# Revit family: Kee_Safety_INTEW010_-_KEELINE_EXTENDED_INT_BRACKET
name_source: partatom
category: Generic Models
units: mm (PartAtom-declared; Revit-internal decimal feet)

## family parameters
Can host rebar = No
Cut with Voids When Loaded = No
Host = Face
Maintain Annotation Orientation = No
Part Type = Normal
Room Calculation Point = No
Round Connector Dimension = Use Diameter
Shared = No

## types (1)
- Kee_Safety_INTEW010_-_KEELINE_EXTENDED_INT_BRACKET
    Assembly Code = INTEW010
    CE Approval = Yes
    Colour = Natural
    Coverage Area = 0 m²
    Default Elevation = 1219 mm
    Design Country = United Kingdom
    Finish = Natural
    Gross Weight kg = 0.63
    Location of Manufacturer = Cradley Heath
    Manufacturer = Kee Safety
    Manufacturer Country = United Kingdom
    Manufacturer Website = www.keesafety.co.uk
    Material = Stainless Steel, Polished
    Overall Height = 88 mm
    Overall Length = 442 mm
    Overall Width = 45 mm  [stored 0.147638 ft]
    Product Family = KeeLine
    Product Group = KeeLine
    Product Model Number = LAINTEXT0
    Product Range = KeeLine
    Shipping Weight kg = 0.0
    Width = 45 mm  [stored 0.147638 ft]

note: [stored X ft] marks values corroborated as IEEE doubles in the binary element streams (Revit-internal decimal feet)

## geometry (parser evidence)
native form markers: Sweep x2
no freeform markers — native parametric forms only
